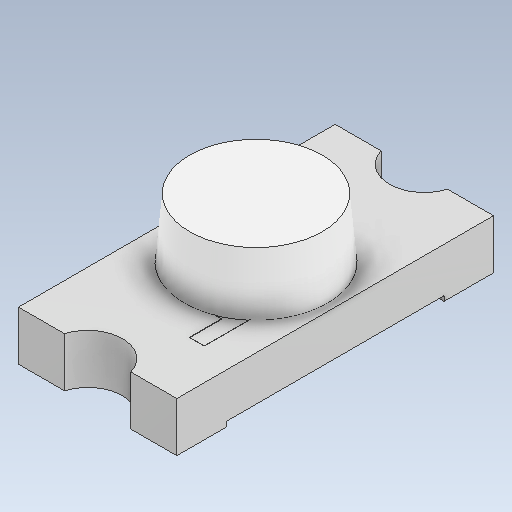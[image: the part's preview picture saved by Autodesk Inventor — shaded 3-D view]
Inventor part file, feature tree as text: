
AUTODESK INVENTOR PART (.ipt)
format: ipt  version: 2020 (Build 240168000, 168)  size: 134,656 bytes
history: native  units: mm
features: other x2, extrude x2
ambient origin geometry x8: Origin, YZ Plane, XZ Plane, XY Plane, X Axis, Y Axis, Z Axis, Center Point
bodies: Body1 (feature_tree), Body2 (feature_tree)
feature tree (4):
  other  "Твердое тело1"
  other  "Твердое тело2"
  extrude  "Extrude2"  [1 undecoded]
  extrude  "Extrude3"  [1 undecoded]
note: 2 required parameter values undecoded (feature->parameter linkage not recoverable at this tier; creation-order binding heuristic only, values carry confidence <= 0.55)
